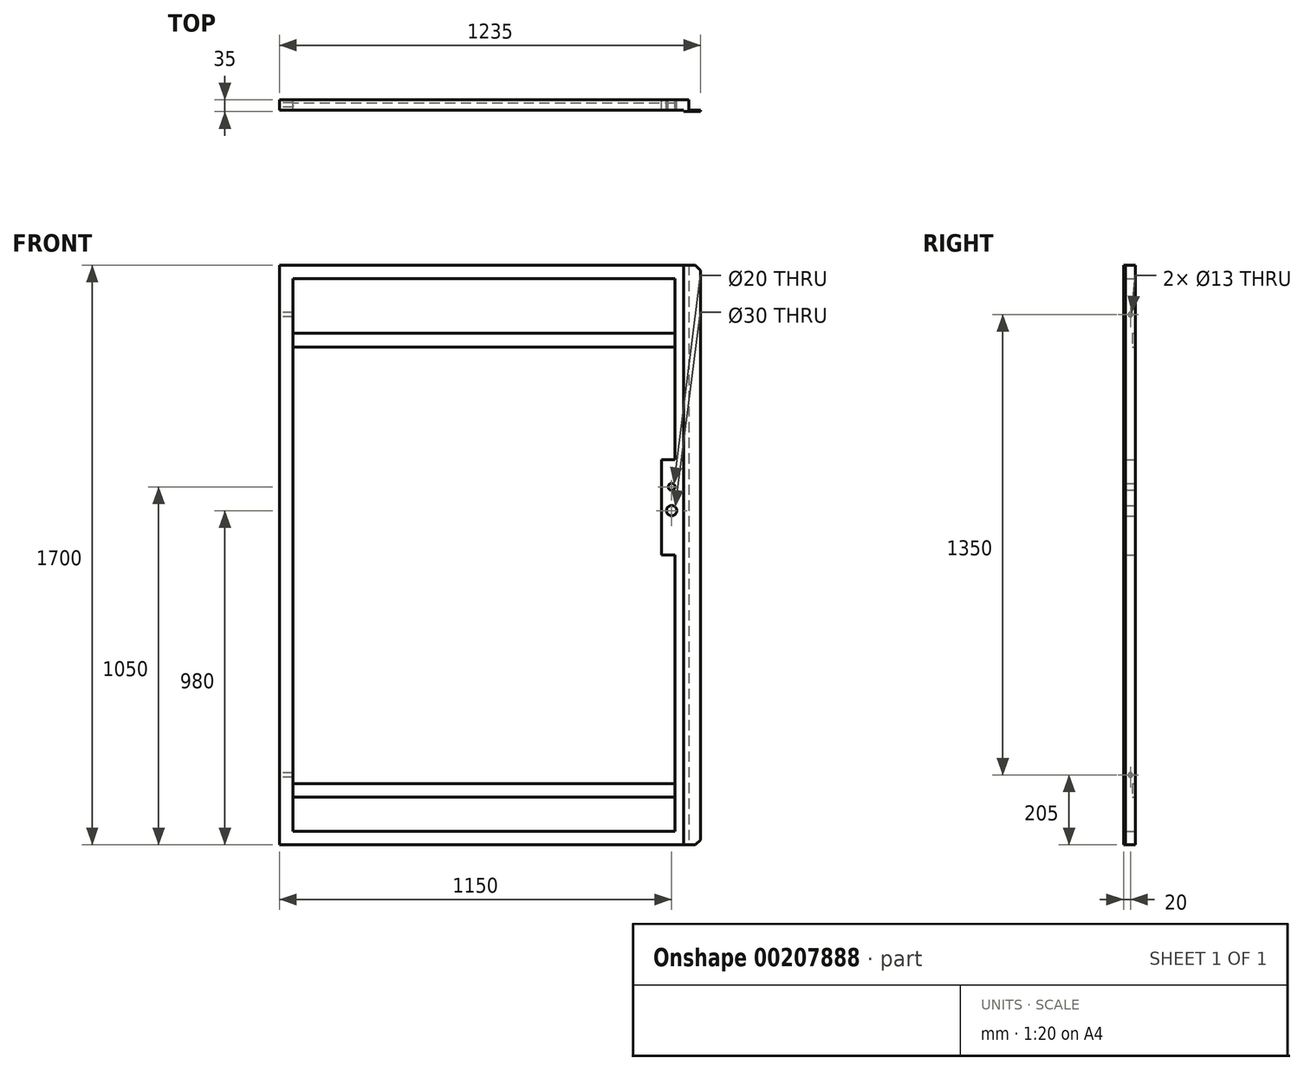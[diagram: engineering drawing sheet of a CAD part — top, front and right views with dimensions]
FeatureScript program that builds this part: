
annotation { "Feature Type Name" : "Feature", "Feature Type Description" : "" }
export const myFeature = defineFeature(function(context is Context, id is Id, definition is map)
    precondition{}
    {
        {
            var Q0;
            Q0=qCreatedBy(makeId("Front.planeOp"),FACE);
            var sketch = newSketch(context, id + "F0", { "sketchPlane" : qUnion([Q0])});
            skLineSegment(sketch, "E0.bottom", {"start": v(-600, 850) * mm, "end": v(600, 850) * mm});
            skLineSegment(sketch, "E0.top", {"start": v(-600, -850) * mm, "end": v(600, -850) * mm});
            skLineSegment(sketch, "E0.left", {"start": v(-600, 850) * mm, "end": v(-600, -850) * mm});
            skLineSegment(sketch, "E0.right", {"start": v(600, 850) * mm, "end": v(600, -850) * mm});
            skLineSegment(sketch, "E1.bottom", {"start": v(-560, 810) * mm, "end": v(560, 810) * mm});
            skLineSegment(sketch, "E1.top", {"start": v(-560, -810) * mm, "end": v(560, -810) * mm});
            skLineSegment(sketch, "E1.left", {"start": v(-560, 810) * mm, "end": v(-560, -810) * mm});
            skLineSegment(sketch, "E1.right", {"start": v(560, 810) * mm, "end": v(560, 280) * mm});
            skLineSegment(sketch, "E2", {"start": v(560, 0) * mm, "end": v(560, -810) * mm});
            skLineSegment(sketch, "E3", {"start": v(560, 280) * mm, "end": v(520, 280) * mm});
            skLineSegment(sketch, "E4", {"start": v(520, 280) * mm, "end": v(520, 0) * mm});
            skLineSegment(sketch, "E5", {"start": v(520, 0) * mm, "end": v(560, 0) * mm});
            skCircle(sketch, "E6", {"center": v(550, 200) * mm, "radius": 10 * mm});
            skCircle(sketch, "E7", {"center": v(550, 130) * mm, "radius": 15 * mm});
            skLineSegment(sketch, "E8", {"start": v(550, 200) * mm, "end": v(550, 130) * mm, "construction": true});
            skSolve(sketch);
        }
        {
            var Q0;
            Q0=makeQuery(id+"F0.imprint","IMPRINT",FACE,{"disambiguationData":[TD([[makeQuery(id+"F0.imprint","IMPRINT",EDGE,{"derivedFrom":sQuery(id+"F0.wireOp",EDGE,"E0.bottom")}),-1.0]])]});
            extrude(context, id + "F1", {"entities" : qUnion([Q0]), "depth" : 30 * mm, "symmetric" : true});
        }
        {
            var Q0;
            Q0=makeQuery(id+"F1.opExtrude","CAP_FACE",FACE,{"disambiguationData":[OSD([sQuery(id+"F0.wireOp",EDGE,"E0.bottom"),sQuery(id+"F0.wireOp",EDGE,"E0.top"),sQuery(id+"F0.wireOp",EDGE,"E0.left"),sQuery(id+"F0.wireOp",EDGE,"E0.right"),sQuery(id+"F0.wireOp",EDGE,"E1.bottom"),sQuery(id+"F0.wireOp",EDGE,"E1.top"),sQuery(id+"F0.wireOp",EDGE,"E1.left"),sQuery(id+"F0.wireOp",EDGE,"E1.right"),sQuery(id+"F0.wireOp",EDGE,"E2"),sQuery(id+"F0.wireOp",EDGE,"E3"),sQuery(id+"F0.wireOp",EDGE,"E4"),sQuery(id+"F0.wireOp",EDGE,"E5"),sQuery(id+"F0.wireOp",EDGE,"E6"),sQuery(id+"F0.wireOp",EDGE,"E7")])],"isStart":true});
            var sketch = newSketch(context, id + "F2", { "sketchPlane" : qUnion([Q0])});
            skLineSegment(sketch, "E9.bottom", {"start": v(-560, 650) * mm, "end": v(560, 650) * mm});
            skLineSegment(sketch, "E9.top", {"start": v(-560, 610) * mm, "end": v(560, 610) * mm});
            skLineSegment(sketch, "E9.left", {"start": v(-560, 650) * mm, "end": v(-560, 610) * mm});
            skLineSegment(sketch, "E9.right", {"start": v(560, 650) * mm, "end": v(560, 610) * mm});
            skLineSegment(sketch, "E10.bottom", {"start": v(560, -710) * mm, "end": v(-560, -710) * mm});
            skLineSegment(sketch, "E10.top", {"start": v(560, -670) * mm, "end": v(-560, -670) * mm});
            skLineSegment(sketch, "E10.left", {"start": v(560, -710) * mm, "end": v(560, -670) * mm});
            skLineSegment(sketch, "E10.right", {"start": v(-560, -710) * mm, "end": v(-560, -670) * mm});
            skSolve(sketch);
        }
        {
            var Q0;
            Q0 = qSketchRegion(id + "F2", true);
            extrude(context, id + "F3", {"entities" : qUnion([Q0]), "operationType" : NewBodyOperationType.ADD, "oppositeDirection" : true, "depth" : 10 * mm});
        }
        {
            var Q0;
            Q0=makeQuery(id+"F1.opExtrude","SWEPT_FACE",FACE,{"disambiguationData":[OSD([sQuery(id+"F0.wireOp",EDGE,"E0.left")])]});
            var sketch = newSketch(context, id + "F4", { "sketchPlane" : qUnion([Q0])});
            skPoint(sketch, "E11", {"position": v(0, -645) * mm});
            skLineSegment(sketch, "E12", {"start": v(0, -645) * mm, "end": v(0, 705) * mm, "construction": true});
            skPoint(sketch, "E13", {"position": v(0, 705) * mm});
            skSolve(sketch);
        }
        {
            var Q0;
            Q0=sQuery(id+"F4.wireOp",VERTEX,"E11");
            var Q1;
            Q1=makeQuery(id+"F1.opExtrude","SWEPT_BODY",BODY,{"disambiguationData":[OSD([sQuery(id+"F0.wireOp",EDGE,"E0.bottom"),sQuery(id+"F0.wireOp",EDGE,"E0.top"),sQuery(id+"F0.wireOp",EDGE,"E0.left"),sQuery(id+"F0.wireOp",EDGE,"E0.right"),sQuery(id+"F0.wireOp",EDGE,"E1.bottom"),sQuery(id+"F0.wireOp",EDGE,"E1.top"),sQuery(id+"F0.wireOp",EDGE,"E1.left"),sQuery(id+"F0.wireOp",EDGE,"E1.right"),sQuery(id+"F0.wireOp",EDGE,"E2"),sQuery(id+"F0.wireOp",EDGE,"E3"),sQuery(id+"F0.wireOp",EDGE,"E4"),sQuery(id+"F0.wireOp",EDGE,"E5"),sQuery(id+"F0.wireOp",EDGE,"E6"),sQuery(id+"F0.wireOp",EDGE,"E7")])]});
            hole(context, id + "F5", {"style" : HoleStyle.SIMPLE, "endStyle" : HoleEndStyle.BLIND, "holeDiameter" : 13 * mm, "holeDepth" : 50 * mm, "startFromSketch" : true, "locations" : qUnion([Q0]), "scope" : qUnion([Q1])});
        }
        {
            var Q0;
            Q0=sQuery(id+"F4.wireOp",VERTEX,"E13");
            var Q1;
            Q1=makeQuery(id+"F1.opExtrude","SWEPT_BODY",BODY,{"disambiguationData":[OSD([sQuery(id+"F0.wireOp",EDGE,"E0.bottom"),sQuery(id+"F0.wireOp",EDGE,"E0.top"),sQuery(id+"F0.wireOp",EDGE,"E0.left"),sQuery(id+"F0.wireOp",EDGE,"E0.right"),sQuery(id+"F0.wireOp",EDGE,"E1.bottom"),sQuery(id+"F0.wireOp",EDGE,"E1.top"),sQuery(id+"F0.wireOp",EDGE,"E1.left"),sQuery(id+"F0.wireOp",EDGE,"E1.right"),sQuery(id+"F0.wireOp",EDGE,"E2"),sQuery(id+"F0.wireOp",EDGE,"E3"),sQuery(id+"F0.wireOp",EDGE,"E4"),sQuery(id+"F0.wireOp",EDGE,"E5"),sQuery(id+"F0.wireOp",EDGE,"E6"),sQuery(id+"F0.wireOp",EDGE,"E7")])]});
            hole(context, id + "F6", {"style" : HoleStyle.SIMPLE, "endStyle" : HoleEndStyle.BLIND, "holeDiameter" : 13 * mm, "holeDepth" : 50 * mm, "startFromSketch" : true, "locations" : qUnion([Q0]), "scope" : qUnion([Q1])});
        }
        {
            var Q0;
            Q0=makeQuery(id+"F1.opExtrude","CAP_FACE",FACE,{"disambiguationData":[OSD([sQuery(id+"F0.wireOp",EDGE,"E0.bottom"),sQuery(id+"F0.wireOp",EDGE,"E0.top"),sQuery(id+"F0.wireOp",EDGE,"E0.left"),sQuery(id+"F0.wireOp",EDGE,"E0.right"),sQuery(id+"F0.wireOp",EDGE,"E1.bottom"),sQuery(id+"F0.wireOp",EDGE,"E1.top"),sQuery(id+"F0.wireOp",EDGE,"E1.left"),sQuery(id+"F0.wireOp",EDGE,"E1.right"),sQuery(id+"F0.wireOp",EDGE,"E2"),sQuery(id+"F0.wireOp",EDGE,"E3"),sQuery(id+"F0.wireOp",EDGE,"E4"),sQuery(id+"F0.wireOp",EDGE,"E5"),sQuery(id+"F0.wireOp",EDGE,"E6"),sQuery(id+"F0.wireOp",EDGE,"E7")])],"isStart":false});
            var sketch = newSketch(context, id + "F7", { "sketchPlane" : qUnion([Q0])});
            skLineSegment(sketch, "E14.bottom", {"start": v(585, 850) * mm, "end": v(635, 850) * mm});
            skLineSegment(sketch, "E14.top", {"start": v(585, -850) * mm, "end": v(635, -850) * mm});
            skLineSegment(sketch, "E14.left", {"start": v(585, 850) * mm, "end": v(585, -850) * mm});
            skLineSegment(sketch, "E14.right", {"start": v(635, 850) * mm, "end": v(635, -850) * mm});
            skSolve(sketch);
        }
        {
            var Q0;
            Q0 = qSketchRegion(id + "F7", true);
            extrude(context, id + "F8", {"entities" : qUnion([Q0]), "operationType" : NewBodyOperationType.ADD, "depth" : 5 * mm});
        }
        {
            var Q0;
            Q0=makeQuery(id+"F8.opExtrude","SWEPT_EDGE",EDGE,{"disambiguationData":[OSD([sQuery(id+"F7.wireOp",EDGE,"E14.top"),sQuery(id+"F7.wireOp",EDGE,"E14.right")])]});
            var Q1;
            Q1=makeQuery(id+"F8.opExtrude","SWEPT_EDGE",EDGE,{"disambiguationData":[OSD([sQuery(id+"F7.wireOp",EDGE,"E14.bottom"),sQuery(id+"F7.wireOp",EDGE,"E14.right")])]});
            chamfer(context, id + "F9", {"entities" : qUnion([Q0, Q1]), "width" : 15 * mm, "tangentPropagation" : true});
        }
    });
